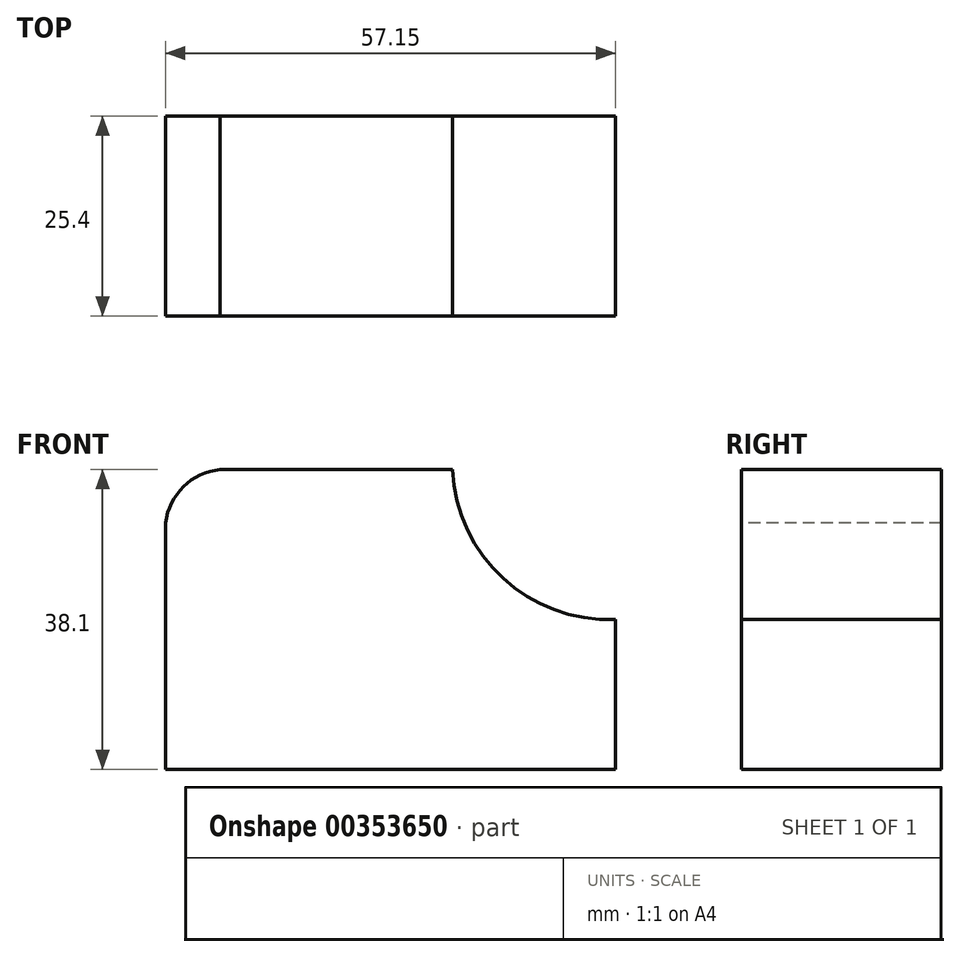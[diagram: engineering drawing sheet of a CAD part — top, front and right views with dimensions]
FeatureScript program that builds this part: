
annotation { "Feature Type Name" : "Feature", "Feature Type Description" : "" }
export const myFeature = defineFeature(function(context is Context, id is Id, definition is map)
    precondition{}
    {
        {
            var Q0;
            Q0=qCreatedBy(makeId("Front.planeOp"),FACE);
            var sketch = newSketch(context, id + "F0", { "sketchPlane" : qUnion([Q0])});
            skLineSegment(sketch, "E0", {"start": v(-57.15, 0) * mm, "end": v(-57.15, 38.1) * mm});
            skLineSegment(sketch, "E1", {"start": v(-57.15, 38.1) * mm, "end": v(0, 38.1) * mm});
            skLineSegment(sketch, "E2", {"start": v(0, 38.1) * mm, "end": v(0, 0) * mm});
            skLineSegment(sketch, "E3", {"start": v(-57.15, 0) * mm, "end": v(0, 0) * mm});
            skSolve(sketch);
        }
        {
            var Q0;
            Q0 = qSketchRegion(id + "F0", true);
            extrude(context, id + "F1", {"entities" : qUnion([Q0]), "depth" : 25.4 * mm});
        }
        {
            var Q0;
            Q0=makeQuery(id+"F1.opExtrude","CAP_FACE",FACE,{"disambiguationData":[OSD([sQuery(id+"F0.wireOp",EDGE,"E0"),sQuery(id+"F0.wireOp",EDGE,"E1"),sQuery(id+"F0.wireOp",EDGE,"E2"),sQuery(id+"F0.wireOp",EDGE,"E3")])],"isStart":false});
            var sketch = newSketch(context, id + "F2", { "sketchPlane" : qUnion([Q0])});
            skArc(sketch, "E4", {"start": v(-48.71, 38.1) * mm, "mid": v(-54.32, 36.42) * mm, "end": v(-57.15, 31.3) * mm});
            skArc(sketch, "E5", {"start": v(-20.7, 38.1) * mm, "mid": v(-14.28, 24.3) * mm, "end": v(0, 19.05) * mm});
            skSolve(sketch);
        }
        {
            var Q0;
            Q0 = qSketchRegion(id + "F2", true);
            var Q1;
            {var subQ0=sQuery(id+"F2.wireOp",EDGE,"E5");Q1=makeQuery(id+"F2.imprint","IMPRINT",FACE,{"disambiguationData":[TD([[makeQuery(id+"F2.imprint","IMPRINT",EDGE,{"derivedFrom":subQ0}),1.0]])]});}
            var Q2;
            {var subQ0=sQuery(id+"F2.wireOp",EDGE,"E4");var subQ1=makeQuery(id+"F1.opExtrude","CAP_EDGE",EDGE,{"disambiguationData":[OSD([sQuery(id+"F0.wireOp",EDGE,"E0")])],"isStart":false});var subQ2=makeQuery(id+"F2.imprint","INTERSECT",VERTEX,{"derivedFrom":[subQ1,subQ0]});Q2=makeQuery(id+"F2.imprint","IMPRINT",FACE,{"disambiguationData":[TD([[makeQuery(id+"F2.imprint","IMPRINT",EDGE,{"disambiguationData":[TD([[subQ2,1.0]])],"derivedFrom":subQ0}),-1.0]])]});}
            extrude(context, id + "F3", {"entities" : qUnion([Q0, Q1, Q2]), "operationType" : NewBodyOperationType.REMOVE, "oppositeDirection" : true, "depth" : 25.4 * mm});
        }
    });
